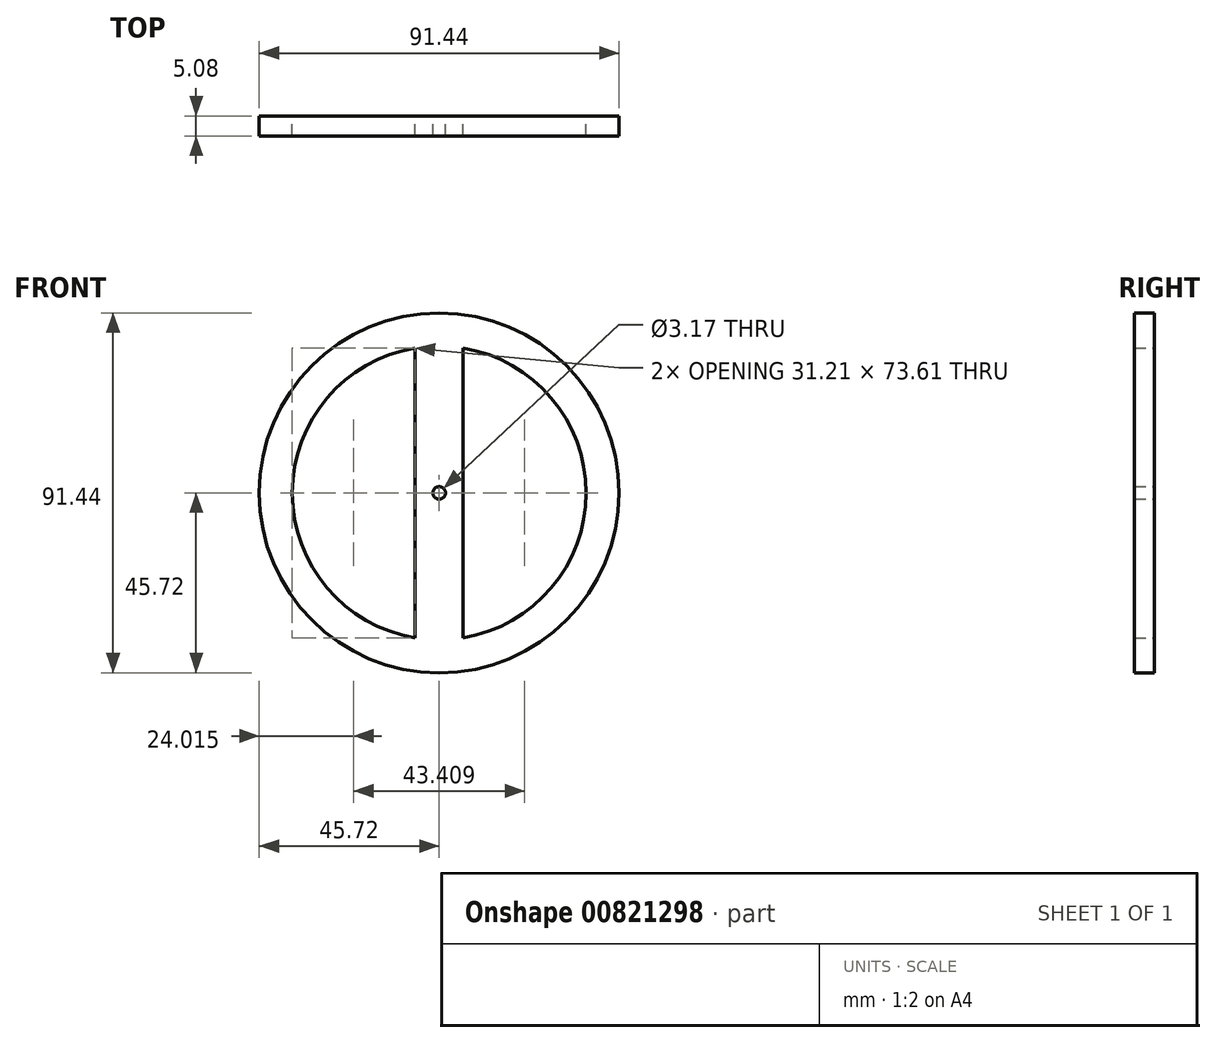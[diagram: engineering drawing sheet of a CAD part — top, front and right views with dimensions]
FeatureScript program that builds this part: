
annotation { "Feature Type Name" : "Feature", "Feature Type Description" : "" }
export const myFeature = defineFeature(function(context is Context, id is Id, definition is map)
    precondition{}
    {
        {
            var Q0;
            Q0=qCreatedBy(makeId("Front.planeOp"),FACE);
            var sketch = newSketch(context, id + "F0", { "sketchPlane" : qUnion([Q0])});
            skCircle(sketch, "E0", {"center": v(0, 0) * mm, "radius": 45.72 * mm});
            skCircle(sketch, "E1", {"center": v(0, 0) * mm, "radius": 37.3 * mm});
            skLineSegment(sketch, "E2.bottom", {"start": v(6.1, 41.4) * mm, "end": v(-6.1, 41.4) * mm});
            skLineSegment(sketch, "E2.top", {"start": v(6.1, -41.4) * mm, "end": v(-6.1, -41.4) * mm});
            skLineSegment(sketch, "E2.left", {"start": v(6.1, 41.4) * mm, "end": v(6.1, -41.4) * mm});
            skLineSegment(sketch, "E2.right", {"start": v(-6.1, 41.4) * mm, "end": v(-6.1, -41.4) * mm});
            skCircle(sketch, "E3", {"center": v(0, 0) * mm, "radius": 1.59 * mm});
            skSolve(sketch);
        }
        {
            var Q0;
            Q0 = qSketchRegion(id + "F0", true);
            var Q1;
            Q1=makeQuery(id+"F0.imprint","IMPRINT",FACE,{"disambiguationData":[TD([[makeQuery(id+"F0.imprint","IMPRINT",EDGE,{"derivedFrom":sQuery(id+"F0.wireOp",EDGE,"E3")}),-1.0]])]});
            var Q2;
            {var subQ5=sQuery(id+"F0.wireOp",EDGE,"E2.bottom");Q2=makeQuery(id+"F0.imprint","IMPRINT",FACE,{"disambiguationData":[TD([[makeQuery(id+"F0.imprint","IMPRINT",EDGE,{"derivedFrom":subQ5}),1.0]])]});}
            var Q3;
            {var subQ5=sQuery(id+"F0.wireOp",EDGE,"E2.top");Q3=makeQuery(id+"F0.imprint","IMPRINT",FACE,{"disambiguationData":[TD([[makeQuery(id+"F0.imprint","IMPRINT",EDGE,{"derivedFrom":subQ5}),-1.0]])]});}
            extrude(context, id + "F1", {"entities" : qUnion([Q0, Q1, Q2, Q3]), "depth" : 5.08 * mm, "offsetDistance" : 25.4 * mm});
        }
    });
